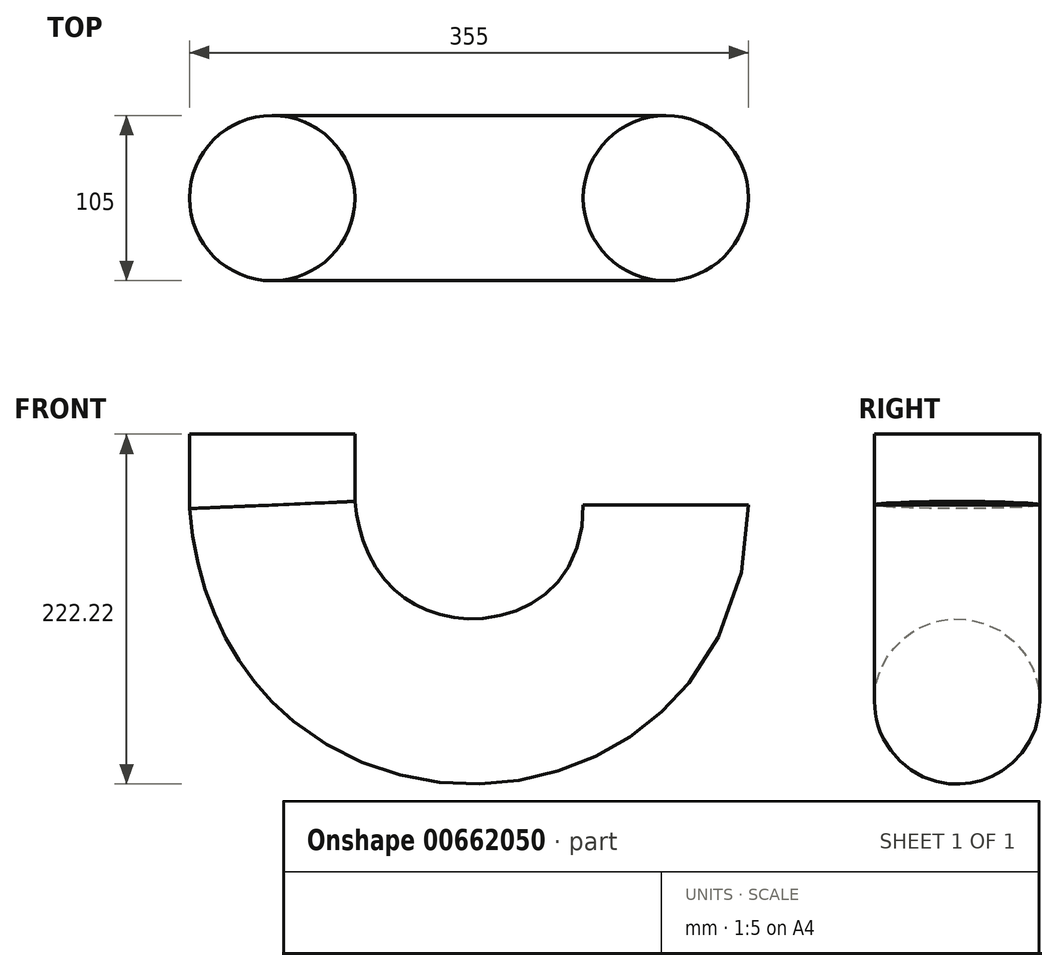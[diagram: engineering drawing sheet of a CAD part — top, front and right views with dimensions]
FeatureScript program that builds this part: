
annotation { "Feature Type Name" : "Feature", "Feature Type Description" : "" }
export const myFeature = defineFeature(function(context is Context, id is Id, definition is map)
    precondition{}
    {
        {
            var Q0;
            Q0=qCreatedBy(makeId("Top.planeOp"),FACE);
            var sketch = newSketch(context, id + "F0", { "sketchPlane" : qUnion([Q0])});
            skCircle(sketch, "E0", {"center": v(0, 0) * mm, "radius": 52.5 * mm});
            skSolve(sketch);
        }
        {
            var Q0;
            Q0=qCreatedBy(makeId("Right.planeOp"),FACE);
            var sketch = newSketch(context, id + "F1", { "sketchPlane" : qUnion([Q0])});
            skLineSegment(sketch, "E1", {"start": v(-74.2, 0) * mm, "end": v(-74.2, -125.37) * mm});
            skLineSegment(sketch, "E2", {"start": v(0, 16.94) * mm, "end": v(250, 16.94) * mm});
            skLineSegment(sketch, "E3", {"start": v(250, 16.94) * mm, "end": v(250, -108.14) * mm});
            skFitSpline(sketch, "E4", {"points": [v(0, 0) * mm, v(250, 0) * mm], "startDerivative": vector(0, -479.27) * mm, "endDerivative": vector(43.55, 518.14) * mm});
            skLineSegment(sketch, "E5", {"start": v(-74.2, -125.37) * mm, "end": v(249.64, -125.37) * mm});
            skLineSegment(sketch, "E6", {"start": v(250, 0) * mm, "end": v(250, 45) * mm});
            skSolve(sketch);
        }
        {
            var Q0;
            Q0=makeQuery(id+"F0.imprint","IMPRINT",FACE,{"disambiguationData":[TD([[makeQuery(id+"F0.imprint","IMPRINT",EDGE,{"derivedFrom":sQuery(id+"F0.wireOp",EDGE,"E0")}),1.0]])]});
            var Q1;
            Q1=sQuery(id+"F1.wireOp",EDGE,"E4");
            var Q2;
            Q2=sQuery(id+"F1.wireOp",EDGE,"E6");
            sweep(context, id + "F2", {"profiles" : qUnion([Q0]), "path" : qUnion([Q1, Q2])});
        }
        {
            var Q0;
            Q0=qCreatedBy(makeId("Front.planeOp"),FACE);
            var sketch = newSketch(context, id + "F3", { "sketchPlane" : qUnion([Q0])});
            skLineSegment(sketch, "E7", {"start": v(0, 109.38) * mm, "end": v(0, -193.98) * mm});
            skSolve(sketch);
        }
        {
            var Q0;
            Q0=makeQuery(id+"F2.opSweep","SWEPT_BODY",BODY,{"disambiguationData":[OSD([sQuery(id+"F0.wireOp",EDGE,"E0"),sQuery(id+"F1.wireOp",EDGE,"E6")])]});
            var Q1;
            Q1=sQuery(id+"F3.wireOp",EDGE,"E7");
            transform(context, id + "F4", {"entities" : qUnion([Q0]), "transformType" : TransformType.ROTATION, "transformAxis" : qUnion([Q1]), "angle" : 270 * degree, "makeCopy" : false});
        }
    });
